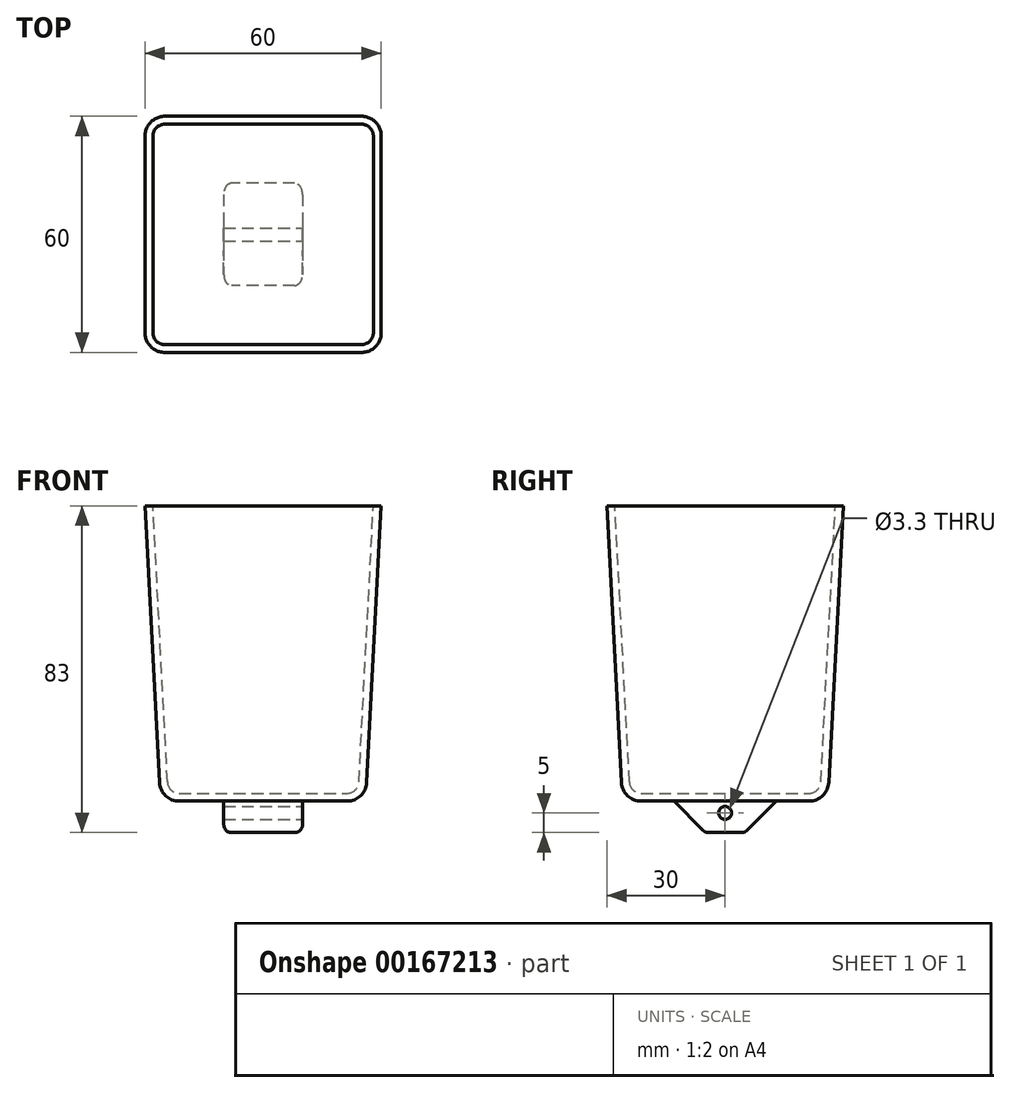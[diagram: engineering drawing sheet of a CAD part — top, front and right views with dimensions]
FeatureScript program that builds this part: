
annotation { "Feature Type Name" : "Feature", "Feature Type Description" : "" }
export const myFeature = defineFeature(function(context is Context, id is Id, definition is map)
    precondition{}
    {
        {
            var Q0;
            Q0=qCreatedBy(makeId("Top.planeOp"),FACE);
            var sketch = newSketch(context, id + "F0", { "sketchPlane" : qUnion([Q0])});
            skLineSegment(sketch, "E0.bottom", {"start": v(30, 30) * mm, "end": v(-30, 30) * mm});
            skLineSegment(sketch, "E0.top", {"start": v(30, -30) * mm, "end": v(-30, -30) * mm});
            skLineSegment(sketch, "E0.left", {"start": v(30, 30) * mm, "end": v(30, -30) * mm});
            skLineSegment(sketch, "E0.right", {"start": v(-30, 30) * mm, "end": v(-30, -30) * mm});
            skPoint(sketch, "E0.middle", {"position": v(0, 0) * mm});
            skSolve(sketch);
        }
        {
            var Q0;
            Q0=makeQuery(id+"F0.imprint","IMPRINT",FACE,{"disambiguationData":[TD([[makeQuery(id+"F0.imprint","IMPRINT",EDGE,{"derivedFrom":sQuery(id+"F0.wireOp",EDGE,"E0.bottom")}),1.0]])]});
            extrude(context, id + "F1", {"entities" : qUnion([Q0]), "oppositeDirection" : true, "depth" : 75 * mm, "hasDraft" : true, "draftAngle" : 3 * degree, "draftPullDirection" : true});
        }
        {
            var Q0;
            Q0=makeQuery(id+"F1.opExtrude","SWEPT_EDGE",EDGE,{"disambiguationData":[OSD([sQuery(id+"F0.wireOp",EDGE,"E0.bottom"),sQuery(id+"F0.wireOp",EDGE,"E0.left")])]});
            var Q1;
            Q1=makeQuery(id+"F5.boolean.opBoolean","MERGE",EDGE,{"derivedFrom":[makeQuery(id+"F1.opExtrude","CAP_EDGE",EDGE,{"disambiguationData":[OSD([sQuery(id+"F0.wireOp",EDGE,"E0.bottom")])],"isStart":false}),makeQuery(id+"F5.opExtrude","TWEAK_EDGE",EDGE,{"derivedFrom":[makeQuery(id+"F4.imprint","IMPRINT",EDGE,{"derivedFrom":sQuery(id+"F4.wireOp",EDGE,"E1")}),makeQuery(id+"F4.imprint","IMPRINT",EDGE,{"derivedFrom":sQuery(id+"F4.wireOp",EDGE,"LCzklbzL-Kmrn-djEx-TaZ7-piAN8hHDd7gp")})]})]});
            var Q2;
            Q2=makeQuery(id+"F1.opExtrude","SWEPT_EDGE",EDGE,{"disambiguationData":[OSD([sQuery(id+"F0.wireOp",EDGE,"E0.bottom"),sQuery(id+"F0.wireOp",EDGE,"E0.right")])]});
            var Q3;
            Q3=makeQuery(id+"F1.opExtrude","SWEPT_EDGE",EDGE,{"disambiguationData":[OSD([sQuery(id+"F0.wireOp",EDGE,"E0.top"),sQuery(id+"F0.wireOp",EDGE,"E0.right")])]});
            var Q4;
            Q4=makeQuery(id+"F1.opExtrude","SWEPT_EDGE",EDGE,{"disambiguationData":[OSD([sQuery(id+"F0.wireOp",EDGE,"E0.top"),sQuery(id+"F0.wireOp",EDGE,"E0.left")])]});
            var Q5;
            Q5=makeQuery(id+"F5.boolean.opBoolean","MERGE",EDGE,{"derivedFrom":[makeQuery(id+"F1.opExtrude","CAP_EDGE",EDGE,{"disambiguationData":[OSD([sQuery(id+"F0.wireOp",EDGE,"E0.top")])],"isStart":false}),makeQuery(id+"F5.opExtrude","TWEAK_EDGE",EDGE,{"derivedFrom":[makeQuery(id+"F4.imprint","IMPRINT",EDGE,{"derivedFrom":sQuery(id+"F4.wireOp",EDGE,"LCzklbzL-Kmrn-djEx-TaZ7-piAN8hHDd7gp")}),makeQuery(id+"F4.imprint","IMPRINT",EDGE,{"derivedFrom":sQuery(id+"F4.wireOp",EDGE,"E2")})]})]});
            var Q6;
            Q6=makeQuery(id+"F1.opExtrude","CAP_FACE",FACE,{"disambiguationData":[OSD([sQuery(id+"F0.wireOp",EDGE,"E0.bottom"),sQuery(id+"F0.wireOp",EDGE,"E0.top"),sQuery(id+"F0.wireOp",EDGE,"E0.left"),sQuery(id+"F0.wireOp",EDGE,"E0.right")])],"isStart":false});
            var Q7;
            Q7=makeQuery(id+"F1.opExtrude","CAP_EDGE",EDGE,{"disambiguationData":[OSD([sQuery(id+"F0.wireOp",EDGE,"E0.left")])],"isStart":false});
            var Q8;
            Q8=makeQuery(id+"F1.opExtrude","CAP_EDGE",EDGE,{"disambiguationData":[OSD([sQuery(id+"F0.wireOp",EDGE,"E0.right")])],"isStart":false});
            fillet(context, id + "F2", {"entities" : qUnion([Q0, Q1, Q2, Q3, Q4, Q5, Q6, Q7, Q8]), "radius" : 5 * mm, "tangentPropagation" : true, "allowEdgeOverflow" : false});
        }
        {
            var Q0;
            Q0=makeQuery(id+"F1.opExtrude","CAP_FACE",FACE,{"disambiguationData":[OSD([sQuery(id+"F0.wireOp",EDGE,"E0.bottom"),sQuery(id+"F0.wireOp",EDGE,"E0.top"),sQuery(id+"F0.wireOp",EDGE,"E0.left"),sQuery(id+"F0.wireOp",EDGE,"E0.right")])],"isStart":true});
            shell(context, id + "F3", {"entities" : qUnion([Q0]), "thickness" : 2 * mm});
        }
        {
            var Q0;
            Q0=qCreatedBy(makeId("Right.planeOp"),FACE);
            var sketch = newSketch(context, id + "F4", { "sketchPlane" : qUnion([Q0])});
            skLineSegment(sketch, "E1", {"start": v(13, -75) * mm, "end": v(5, -83) * mm});
            skLineSegment(sketch, "E2", {"start": v(-13, -75) * mm, "end": v(-5, -83) * mm});
            skPoint(sketch, "E3", {"position": v(0, -78) * mm});
            skLineSegment(sketch, "E4", {"start": v(5, -83) * mm, "end": v(-5, -83) * mm});
            skLineSegment(sketch, "E5", {"start": v(13, -75) * mm, "end": v(-13, -75) * mm});
            skPoint(sketch, "E6", {"position": v(0, -83) * mm});
            skSolve(sketch);
        }
        {
            var Q0;
            Q0=makeQuery(id+"F4.imprint","IMPRINT",FACE,{"disambiguationData":[TD([[makeQuery(id+"F4.imprint","IMPRINT",EDGE,{"derivedFrom":sQuery(id+"F4.wireOp",EDGE,"E1")}),-1.0]])]});
            var Q1;
            Q1=makeQuery(id+"F1.opExtrude","SWEPT_FACE",FACE,{"disambiguationData":[OSD([sQuery(id+"F0.wireOp",EDGE,"E0.left")])]});
            var Q2;
            Q2=makeQuery(id+"F1.opExtrude","SWEPT_FACE",FACE,{"disambiguationData":[OSD([sQuery(id+"F0.wireOp",EDGE,"E0.right")])]});
            extrude(context, id + "F5", {"entities" : qUnion([Q0]), "operationType" : NewBodyOperationType.ADD, "endBound" : BoundingType.SYMMETRIC, "endBoundEntityFace" : qUnion([Q1]), "depth" : 20 * mm, "hasSecondDirection" : true, "secondDirectionBound" : SecondDirectionBoundingType.UP_TO_SURFACE, "secondDirectionOppositeDirection" : true, "secondDirectionBoundEntityFace" : qUnion([Q2]), "secondDirectionDepth" : 25 * mm});
        }
        {
            var Q0;
            Q0=makeQuery(id+"F5.opExtrude","CAP_EDGE",EDGE,{"disambiguationData":[OSD([sQuery(id+"F4.wireOp",EDGE,"E2")])],"isStart":true});
            var Q1;
            Q1=makeQuery(id+"F5.opExtrude","CAP_EDGE",EDGE,{"disambiguationData":[OSD([sQuery(id+"F4.wireOp",EDGE,"E4")])],"isStart":true});
            var Q2;
            Q2=makeQuery(id+"F5.opExtrude","CAP_EDGE",EDGE,{"disambiguationData":[OSD([sQuery(id+"F4.wireOp",EDGE,"E1")])],"isStart":true});
            var Q3;
            Q3=makeQuery(id+"F5.opExtrude","CAP_EDGE",EDGE,{"disambiguationData":[OSD([sQuery(id+"F4.wireOp",EDGE,"E1")])],"isStart":false});
            var Q4;
            Q4=makeQuery(id+"F5.opExtrude","CAP_EDGE",EDGE,{"disambiguationData":[OSD([sQuery(id+"F4.wireOp",EDGE,"E4")])],"isStart":false});
            var Q5;
            Q5=makeQuery(id+"F5.opExtrude","CAP_EDGE",EDGE,{"disambiguationData":[OSD([sQuery(id+"F4.wireOp",EDGE,"E2")])],"isStart":false});
            var Q6;
            Q6=makeQuery(id+"F5.opExtrude","SWEPT_EDGE",EDGE,{"disambiguationData":[OSD([sQuery(id+"F4.wireOp",EDGE,"E2"),sQuery(id+"F4.wireOp",EDGE,"E4")])]});
            var Q7;
            Q7=makeQuery(id+"F5.opExtrude","SWEPT_EDGE",EDGE,{"disambiguationData":[OSD([sQuery(id+"F4.wireOp",EDGE,"E1"),sQuery(id+"F4.wireOp",EDGE,"E4")])]});
            fillet(context, id + "F6", {"entities" : qUnion([Q0, Q1, Q2, Q3, Q4, Q5, Q6, Q7]), "radius" : 2 * mm, "tangentPropagation" : true, "allowEdgeOverflow" : false});
        }
        {
            var Q0;
            Q0=sQuery(id+"F4.wireOp",VERTEX,"E3");
            var Q1;
            Q1=makeQuery(id+"F1.opExtrude","SWEPT_BODY",BODY,{"disambiguationData":[OSD([sQuery(id+"F0.wireOp",EDGE,"E0.bottom"),sQuery(id+"F0.wireOp",EDGE,"E0.top"),sQuery(id+"F0.wireOp",EDGE,"E0.left"),sQuery(id+"F0.wireOp",EDGE,"E0.right")])]});
            hole(context, id + "F7", {"style" : HoleStyle.SIMPLE, "endStyle" : HoleEndStyle.THROUGH, "holeDiameter" : 3.3 * mm, "locations" : qUnion([Q0]), "scope" : qUnion([Q1]), "isTappedThrough" : true});
        }
        {
            var Q0;
            Q0=sQuery(id+"F4.wireOp",VERTEX,"E3");
            var Q1;
            Q1=makeQuery(id+"F1.opExtrude","SWEPT_BODY",BODY,{"disambiguationData":[OSD([sQuery(id+"F0.wireOp",EDGE,"E0.bottom"),sQuery(id+"F0.wireOp",EDGE,"E0.top"),sQuery(id+"F0.wireOp",EDGE,"E0.left"),sQuery(id+"F0.wireOp",EDGE,"E0.right")])]});
            hole(context, id + "F8", {"style" : HoleStyle.SIMPLE, "endStyle" : HoleEndStyle.THROUGH, "oppositeDirection" : true, "holeDiameter" : 3.3 * mm, "locations" : qUnion([Q0]), "scope" : qUnion([Q1]), "isTappedThrough" : true});
        }
    });
